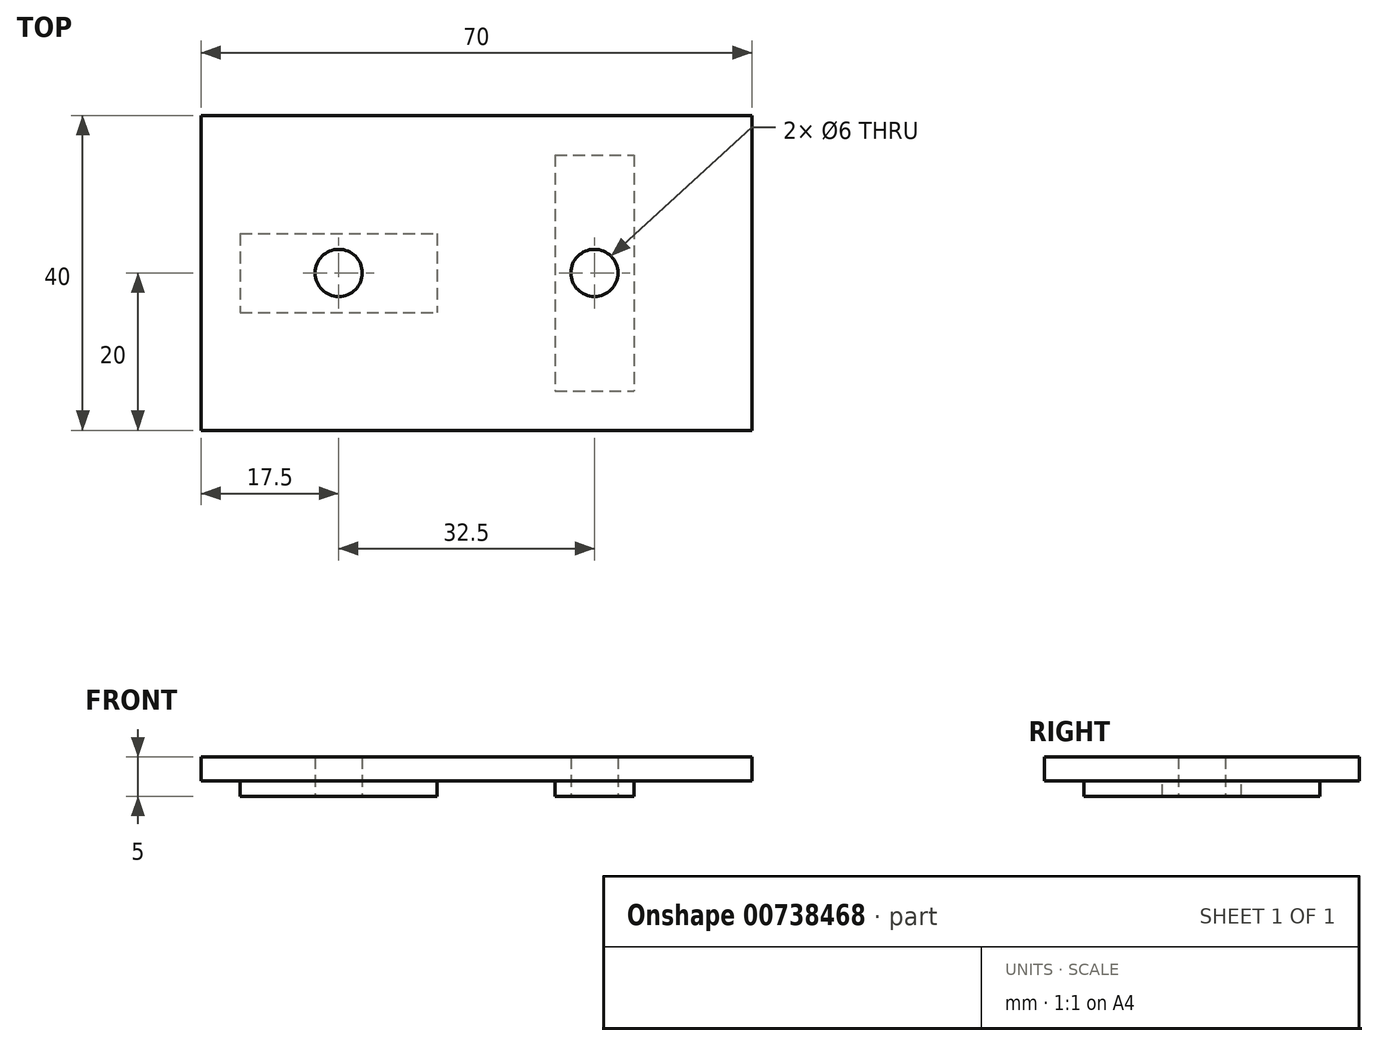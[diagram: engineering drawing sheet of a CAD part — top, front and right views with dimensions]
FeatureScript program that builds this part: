
annotation { "Feature Type Name" : "Feature", "Feature Type Description" : "" }
export const myFeature = defineFeature(function(context is Context, id is Id, definition is map)
    precondition{}
    {
        {
            var Q0;
            Q0=qCreatedBy(makeId("Top.planeOp"),FACE);
            var sketch = newSketch(context, id + "F0", { "sketchPlane" : qUnion([Q0])});
            skLineSegment(sketch, "E0.bottom", {"start": v(35, 20) * mm, "end": v(-35, 20) * mm});
            skLineSegment(sketch, "E0.top", {"start": v(35, -20) * mm, "end": v(-35, -20) * mm});
            skLineSegment(sketch, "E0.left", {"start": v(35, 20) * mm, "end": v(35, -20) * mm});
            skLineSegment(sketch, "E0.right", {"start": v(-35, 20) * mm, "end": v(-35, -20) * mm});
            skPoint(sketch, "E0.middle", {"position": v(0, 0) * mm});
            skLineSegment(sketch, "E1.bottom", {"start": v(10, 15) * mm, "end": v(20, 15) * mm});
            skLineSegment(sketch, "E1.top", {"start": v(10, -15) * mm, "end": v(20, -15) * mm});
            skLineSegment(sketch, "E1.left", {"start": v(10, 15) * mm, "end": v(10, -15) * mm});
            skLineSegment(sketch, "E1.right", {"start": v(20, 15) * mm, "end": v(20, -15) * mm});
            skLineSegment(sketch, "E2.bottom", {"start": v(-30, 5) * mm, "end": v(-5, 5) * mm});
            skLineSegment(sketch, "E2.top", {"start": v(-30, -5) * mm, "end": v(-5, -5) * mm});
            skLineSegment(sketch, "E2.left", {"start": v(-30, 5) * mm, "end": v(-30, -5) * mm});
            skLineSegment(sketch, "E2.right", {"start": v(-5, 5) * mm, "end": v(-5, -5) * mm});
            skSolve(sketch);
        }
        {
            var Q0;
            Q0=makeQuery(id+"F0.imprint","IMPRINT",FACE,{"disambiguationData":[TD([[makeQuery(id+"F0.imprint","IMPRINT",EDGE,{"derivedFrom":sQuery(id+"F0.wireOp",EDGE,"E0.bottom")}),1.0]])]});
            var Q1;
            Q1=makeQuery(id+"F0.imprint","IMPRINT",FACE,{"disambiguationData":[TD([[makeQuery(id+"F0.imprint","IMPRINT",EDGE,{"derivedFrom":sQuery(id+"F0.wireOp",EDGE,"E2.bottom")}),-1.0]])]});
            var Q2;
            Q2=makeQuery(id+"F0.imprint","IMPRINT",FACE,{"disambiguationData":[TD([[makeQuery(id+"F0.imprint","IMPRINT",EDGE,{"derivedFrom":sQuery(id+"F0.wireOp",EDGE,"E1.bottom")}),-1.0]])]});
            extrude(context, id + "F1", {"entities" : qUnion([Q0, Q1, Q2]), "depth" : 3 * mm, "offsetDistance" : 25 * mm});
        }
        {
            var Q0;
            Q0=makeQuery(id+"F0.imprint","IMPRINT",FACE,{"disambiguationData":[TD([[makeQuery(id+"F0.imprint","IMPRINT",EDGE,{"derivedFrom":sQuery(id+"F0.wireOp",EDGE,"E2.bottom")}),-1.0]])]});
            var Q1;
            Q1=makeQuery(id+"F0.imprint","IMPRINT",FACE,{"disambiguationData":[TD([[makeQuery(id+"F0.imprint","IMPRINT",EDGE,{"derivedFrom":sQuery(id+"F0.wireOp",EDGE,"E1.bottom")}),-1.0]])]});
            extrude(context, id + "F2", {"entities" : qUnion([Q0, Q1]), "operationType" : NewBodyOperationType.ADD, "oppositeDirection" : true, "depth" : 2 * mm, "offsetDistance" : 25 * mm});
        }
        {
            var Q0;
            Q0=makeQuery(id+"F2.opExtrude","CAP_FACE",FACE,{"disambiguationData":[OSD([sQuery(id+"F0.wireOp",EDGE,"E2.bottom"),sQuery(id+"F0.wireOp",EDGE,"E2.top"),sQuery(id+"F0.wireOp",EDGE,"E2.left"),sQuery(id+"F0.wireOp",EDGE,"E2.right")])],"isStart":false});
            var sketch = newSketch(context, id + "F3", { "sketchPlane" : qUnion([Q0])});
            skLineSegment(sketch, "E3", {"start": v(-30, -5) * mm, "end": v(-5, 5) * mm, "construction": true});
            skLineSegment(sketch, "E4", {"start": v(-30, 5) * mm, "end": v(-5, -5) * mm, "construction": true});
            skCircle(sketch, "E5", {"center": v(-17.5, 0) * mm, "radius": 3 * mm});
            skSolve(sketch);
        }
        {
            var Q0;
            Q0=makeQuery(id+"F2.opExtrude","CAP_FACE",FACE,{"disambiguationData":[OSD([sQuery(id+"F0.wireOp",EDGE,"E1.bottom"),sQuery(id+"F0.wireOp",EDGE,"E1.top"),sQuery(id+"F0.wireOp",EDGE,"E1.left"),sQuery(id+"F0.wireOp",EDGE,"E1.right")])],"isStart":false});
            var sketch = newSketch(context, id + "F4", { "sketchPlane" : qUnion([Q0])});
            skLineSegment(sketch, "E6", {"start": v(10, 15) * mm, "end": v(20, -15) * mm, "construction": true});
            skLineSegment(sketch, "E7", {"start": v(20, -15) * mm, "end": v(20, 15) * mm, "construction": true});
            skLineSegment(sketch, "E8", {"start": v(20, 15) * mm, "end": v(10, -15) * mm, "construction": true});
            skCircle(sketch, "E9", {"center": v(15, 0) * mm, "radius": 3 * mm});
            skSolve(sketch);
        }
        {
            var Q0;
            Q0=makeQuery(id+"F3.imprint","IMPRINT",FACE,{"disambiguationData":[TD([[makeQuery(id+"F3.imprint","IMPRINT",EDGE,{"derivedFrom":sQuery(id+"F3.wireOp",EDGE,"E5")}),1.0]])]});
            var Q1;
            Q1=makeQuery(id+"F4.imprint","IMPRINT",FACE,{"disambiguationData":[TD([[makeQuery(id+"F4.imprint","IMPRINT",EDGE,{"derivedFrom":sQuery(id+"F4.wireOp",EDGE,"E9")}),1.0]])]});
            extrude(context, id + "F5", {"entities" : qUnion([Q0, Q1]), "operationType" : NewBodyOperationType.REMOVE, "oppositeDirection" : true, "depth" : 25 * mm, "offsetDistance" : 25 * mm});
        }
    });
